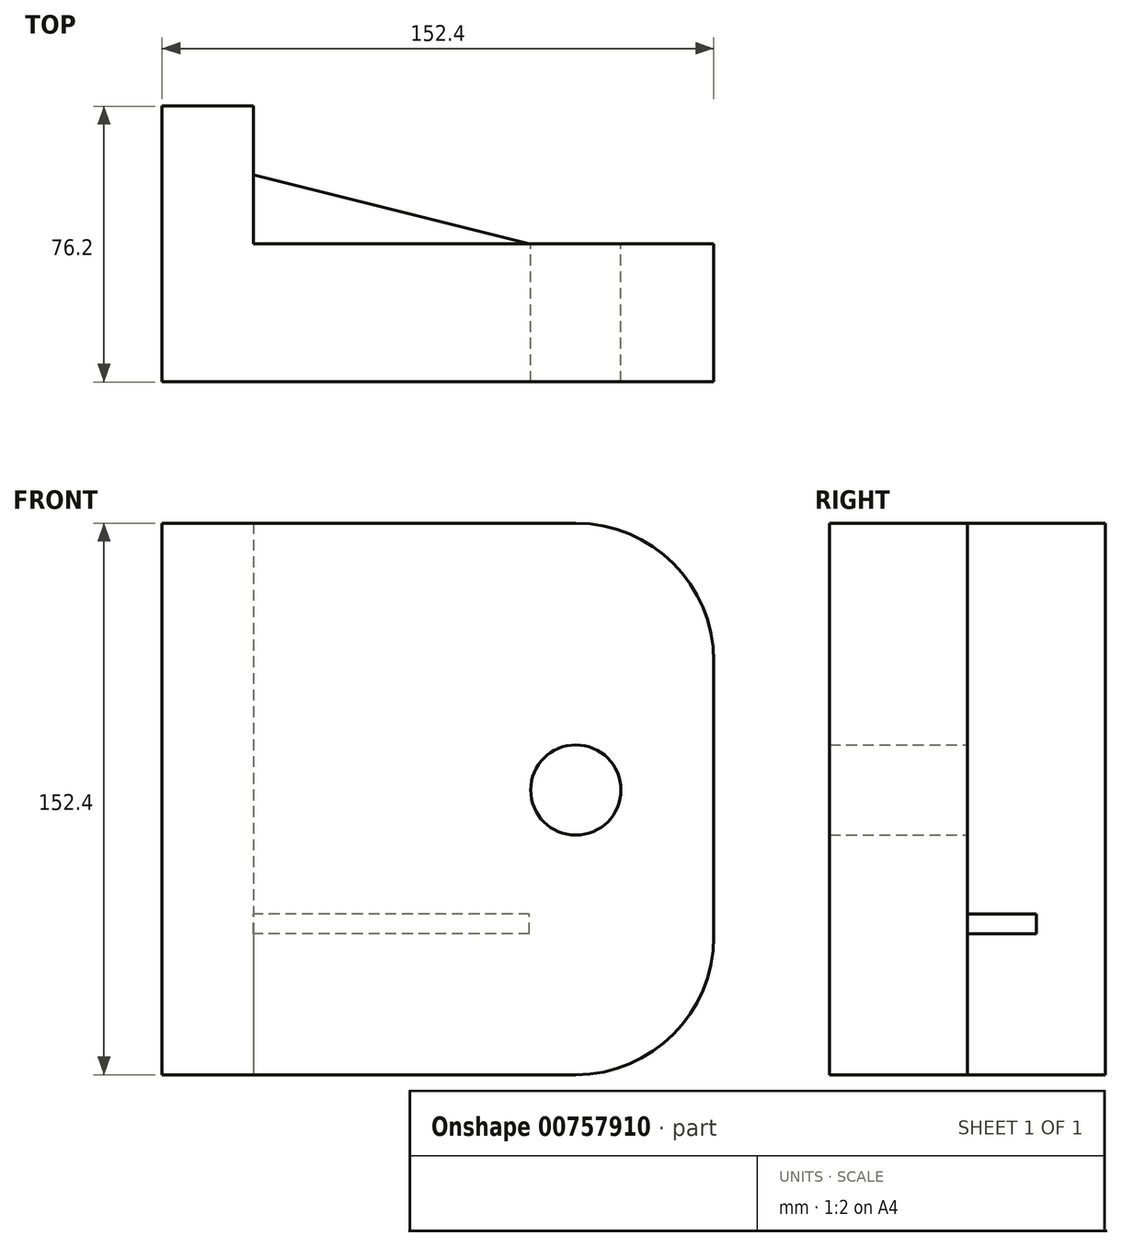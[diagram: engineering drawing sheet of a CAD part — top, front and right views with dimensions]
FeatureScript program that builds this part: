
annotation { "Feature Type Name" : "Feature", "Feature Type Description" : "" }
export const myFeature = defineFeature(function(context is Context, id is Id, definition is map)
    precondition{}
    {
        {
            var Q0;
            Q0=qCreatedBy(makeId("Top.planeOp"),FACE);
            var sketch = newSketch(context, id + "F0", { "sketchPlane" : qUnion([Q0])});
            skLineSegment(sketch, "E0", {"start": v(-90.15, 34.31) * mm, "end": v(-90.15, -41.89) * mm});
            skLineSegment(sketch, "E1", {"start": v(-90.15, -41.89) * mm, "end": v(62.25, -41.89) * mm});
            skLineSegment(sketch, "E2", {"start": v(62.25, -41.89) * mm, "end": v(62.25, -3.79) * mm});
            skLineSegment(sketch, "E3", {"start": v(62.25, -3.79) * mm, "end": v(-64.88, -3.79) * mm});
            skLineSegment(sketch, "E4", {"start": v(-64.88, -3.79) * mm, "end": v(-64.88, 34.31) * mm});
            skLineSegment(sketch, "E5", {"start": v(-64.88, 34.31) * mm, "end": v(-90.15, 34.31) * mm});
            skSolve(sketch);
        }
        {
            var Q0;
            Q0=makeQuery(id+"F0.imprint","IMPRINT",FACE,{"disambiguationData":[TD([[makeQuery(id+"F0.imprint","IMPRINT",EDGE,{"derivedFrom":sQuery(id+"F0.wireOp",EDGE,"E0")}),1.0]])]});
            extrude(context, id + "F1", {"entities" : qUnion([Q0]), "depth" : 152.4 * mm, "offsetDistance" : 25 * mm});
        }
        {
            var Q0;
            Q0=qCreatedBy(makeId("Front.planeOp"),FACE);
            var sketch = newSketch(context, id + "F2", { "sketchPlane" : qUnion([Q0])});
            skCircle(sketch, "E6", {"center": v(24.15, 78.67) * mm, "radius": 12.47 * mm});
            skSolve(sketch);
        }
        {
            var Q0;
            Q0=makeQuery(id+"F2.imprint","IMPRINT",FACE,{"disambiguationData":[TD([[makeQuery(id+"F2.imprint","IMPRINT",EDGE,{"derivedFrom":sQuery(id+"F2.wireOp",EDGE,"E6")}),1.0]])]});
            extrude(context, id + "F3", {"entities" : qUnion([Q0]), "operationType" : NewBodyOperationType.REMOVE, "endBound" : BoundingType.THROUGH_ALL, "depth" : 25 * mm, "offsetDistance" : 25 * mm});
        }
        {
            var Q0;
            Q0=makeQuery(id+"F1.opExtrude","CAP_EDGE",EDGE,{"disambiguationData":[OSD([sQuery(id+"F0.wireOp",EDGE,"E2")])],"isStart":false});
            fillet(context, id + "F4", {"entities" : qUnion([Q0]), "radius" : 38.1 * mm, "tangentPropagation" : true, "allowEdgeOverflow" : false});
        }
        {
            var Q0;
            Q0=makeQuery(id+"F1.opExtrude","CAP_EDGE",EDGE,{"disambiguationData":[OSD([sQuery(id+"F0.wireOp",EDGE,"E2")])],"isStart":true});
            fillet(context, id + "F5", {"entities" : qUnion([Q0]), "radius" : 38.1 * mm, "tangentPropagation" : true, "allowEdgeOverflow" : false});
        }
        {
            var Q0;
            Q0=qCreatedBy(makeId("Top.planeOp"),FACE);
            cPlane(context, id + "F6", {"entities" : qUnion([Q0]), "cplaneType" : CPlaneType.OFFSET, "offset" : 44.45 * mm, "width" : 150 * mm, "height" : 150 * mm});
        }
        {
            var Q0;
            Q0=qCreatedBy(id+"F6.planeOp",FACE);
            var sketch = newSketch(context, id + "F7", { "sketchPlane" : qUnion([Q0])});
            skLineSegment(sketch, "E7.0.1", {"start": v(62.25, -3.79) * mm, "end": v(24.15, -3.79) * mm});
            skLineSegment(sketch, "E7.0.2", {"start": v(24.15, -3.79) * mm, "end": v(-64.88, -3.79) * mm});
            skLineSegment(sketch, "E7.0.4", {"start": v(-64.88, -3.79) * mm, "end": v(24.15, -3.79) * mm});
            skLineSegment(sketch, "E7.0.5", {"start": v(24.15, -3.79) * mm, "end": v(62.25, -3.79) * mm});
            skLineSegment(sketch, "E8.0.0", {"start": v(-64.88, -3.79) * mm, "end": v(-64.88, 34.31) * mm});
            skLineSegment(sketch, "E8.0.2", {"start": v(-64.88, 34.31) * mm, "end": v(-64.88, -3.79) * mm});
            skLineSegment(sketch, "E9", {"start": v(11.32, -3.79) * mm, "end": v(-64.88, 15.26) * mm});
            skSolve(sketch);
        }
        {
            var Q0;
            {var subQ3=sQuery(id+"F7.wireOp",EDGE,"E9");Q0=makeQuery(id+"F7.imprint","IMPRINT",FACE,{"disambiguationData":[TD([[makeQuery(id+"F7.imprint","IMPRINT",EDGE,{"derivedFrom":subQ3}),1.0]])]});}
            extrude(context, id + "F8", {"entities" : qUnion([Q0]), "operationType" : NewBodyOperationType.ADD, "oppositeDirection" : true, "depth" : 5.47 * mm, "offsetDistance" : 25 * mm});
        }
        {
            var Q0;
            Q0=qCreatedBy(id+"F6.planeOp",FACE);
            cPlane(context, id + "F9", {"entities" : qUnion([Q0]), "cplaneType" : CPlaneType.OFFSET, "offset" : 65.48 * mm, "width" : 150 * mm, "height" : 150 * mm});
        }
    });
